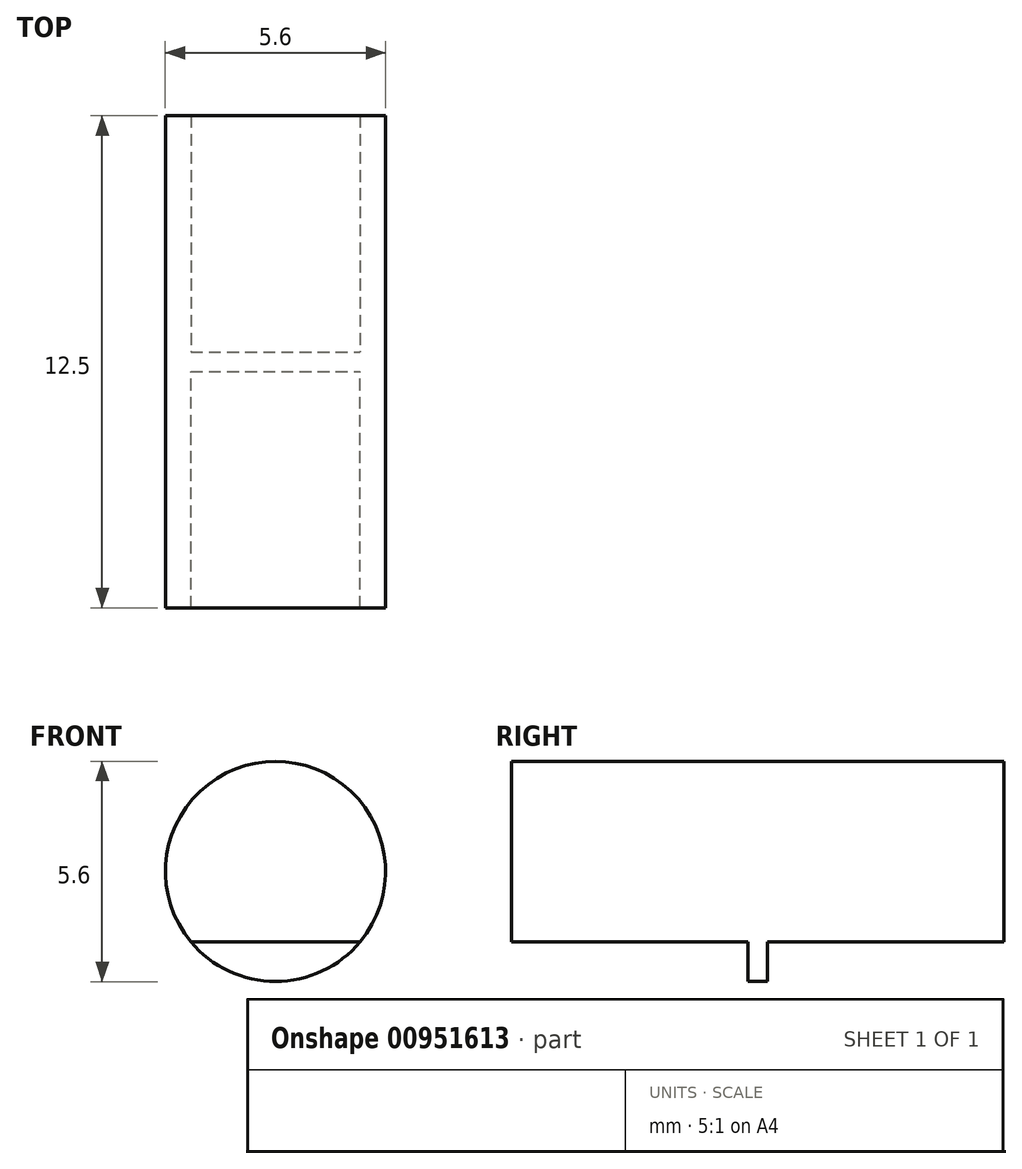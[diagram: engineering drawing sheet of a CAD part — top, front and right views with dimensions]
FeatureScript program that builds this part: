
annotation { "Feature Type Name" : "Feature", "Feature Type Description" : "" }
export const myFeature = defineFeature(function(context is Context, id is Id, definition is map)
    precondition{}
    {
        {
            var Q0;
            Q0=qCreatedBy(makeId("Front.planeOp"),FACE);
            var sketch = newSketch(context, id + "F0", { "sketchPlane" : qUnion([Q0])});
            skCircle(sketch, "E0", {"center": v(0, 0) * mm, "radius": 2.8 * mm});
            skPoint(sketch, "E1", {"position": v(-2.15, -1.79) * mm});
            skPoint(sketch, "E2", {"position": v(2.15, -1.79) * mm});
            skLineSegment(sketch, "E3", {"start": v(-2.15, -1.79) * mm, "end": v(2.15, -1.79) * mm});
            skSolve(sketch);
        }
        {
            assignVariable(context, id + "F1", {"name" : "Shaft_Length", "anyValue" : 0.5});
        }
        {
            var Q0;
            {var subQ0=sQuery(id+"F0.wireOp",EDGE,"E3");Q0=makeQuery(id+"F0.imprint","IMPRINT",FACE,{"disambiguationData":[TD([[makeQuery(id+"F0.imprint","IMPRINT",EDGE,{"derivedFrom":subQ0}),1.0]])]});}
            extrude(context, id + "F2", {"entities" : qUnion([Q0]), "depth" : 6 * mm, "offsetDistance" : 25 * mm});
        }
        {
            var Q0;
            Q0=qSketchRegion(id+"F0",true);
            extrude(context, id + "F3", {"entities" : qUnion([Q0]), "operationType" : NewBodyOperationType.ADD, "oppositeDirection" : true, "depth" : (getVariable(context, 'Shaft_Length')) * mm, "offsetDistance" : 25 * mm});
        }
        {
            var Q0;
            Q0=makeQuery(id+"F3.opExtrude","CAP_FACE",FACE,{"disambiguationData":[OSD([sQuery(id+"F0.wireOp",EDGE,"E0")])],"isStart":false});
            var sketch = newSketch(context, id + "F4", { "sketchPlane" : qUnion([Q0])});
            skArc(sketch, "E4.0.0", {"start": v(-2.15, -1.79) * mm, "mid": v(0, 2.8) * mm, "end": v(2.15, -1.79) * mm});
            skLineSegment(sketch, "E4.0.1", {"start": v(2.15, -1.79) * mm, "end": v(-2.15, -1.79) * mm});
            skSolve(sketch);
        }
        {
            var Q0;
            Q0=qSketchRegion(id+"F4",true);
            extrude(context, id + "F5", {"entities" : qUnion([Q0]), "operationType" : NewBodyOperationType.ADD, "depth" : 6 * mm, "offsetDistance" : 25 * mm});
        }
    });
